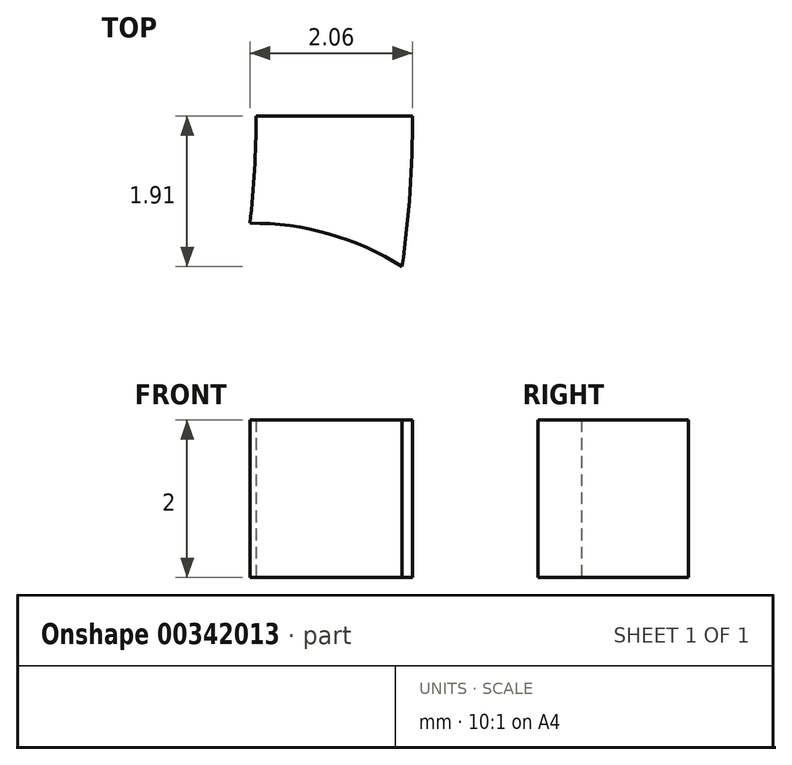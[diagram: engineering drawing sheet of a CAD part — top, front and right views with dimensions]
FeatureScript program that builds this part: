
annotation { "Feature Type Name" : "Feature", "Feature Type Description" : "" }
export const myFeature = defineFeature(function(context is Context, id is Id, definition is map)
    precondition{}
    {
        {
            var Q0;
            Q0=qCreatedBy(makeId("Top.planeOp"),FACE);
            var sketch = newSketch(context, id + "F0", { "sketchPlane" : qUnion([Q0])});
            skCircle(sketch, "E0", {"center": v(4.55, -3.95) * mm, "radius": 13.88 * mm});
            skLineSegment(sketch, "E1", {"start": v(4.55, -17.84) * mm, "end": v(4.55, 9.93) * mm});
            skLineSegment(sketch, "E2", {"start": v(-9.33, -3.95) * mm, "end": v(18.43, -3.95) * mm});
            skLineSegment(sketch, "E3", {"start": v(-9.33, -3.95) * mm, "end": v(4.55, -17.84) * mm});
            skLineSegment(sketch, "E4", {"start": v(4.55, -17.84) * mm, "end": v(18.43, -3.95) * mm});
            skLineSegment(sketch, "E5", {"start": v(18.43, -3.95) * mm, "end": v(4.55, 9.93) * mm});
            skLineSegment(sketch, "E6", {"start": v(4.55, 9.93) * mm, "end": v(-9.33, -3.95) * mm});
            skLineSegment(sketch, "E7", {"start": v(4.55, -3.95) * mm, "end": v(14.37, -13.77) * mm});
            skLineSegment(sketch, "E8", {"start": v(4.55, -3.95) * mm, "end": v(-5.27, 5.86) * mm});
            skLineSegment(sketch, "E9", {"start": v(4.55, -3.95) * mm, "end": v(-5.27, -13.77) * mm});
            skLineSegment(sketch, "E10", {"start": v(-5.27, -13.77) * mm, "end": v(4.55, -3.95) * mm});
            skLineSegment(sketch, "E11", {"start": v(4.55, -3.95) * mm, "end": v(14.37, 5.86) * mm});
            skLineSegment(sketch, "E12", {"start": v(-5.27, -13.77) * mm, "end": v(4.55, -17.84) * mm});
            skLineSegment(sketch, "E13", {"start": v(4.55, -17.84) * mm, "end": v(14.37, -13.77) * mm});
            skLineSegment(sketch, "E14", {"start": v(14.37, -13.77) * mm, "end": v(18.43, -3.95) * mm});
            skLineSegment(sketch, "E15", {"start": v(18.43, -3.95) * mm, "end": v(14.37, 5.86) * mm});
            skLineSegment(sketch, "E16", {"start": v(14.37, 5.86) * mm, "end": v(4.55, 9.93) * mm});
            skLineSegment(sketch, "E17", {"start": v(4.55, 9.93) * mm, "end": v(-5.27, 5.86) * mm});
            skLineSegment(sketch, "E18", {"start": v(-5.27, 5.86) * mm, "end": v(-9.33, -3.95) * mm});
            skLineSegment(sketch, "E19", {"start": v(-9.33, -3.95) * mm, "end": v(-5.27, -13.77) * mm});
            skCircle(sketch, "E20", {"center": v(9.46, -15.8) * mm, "radius": 3.55 * mm});
            skCircle(sketch, "E21", {"center": v(-0.36, -15.8) * mm, "radius": 3.55 * mm});
            skCircle(sketch, "E22", {"center": v(-7.3, -8.86) * mm, "radius": 3.55 * mm});
            skCircle(sketch, "E23", {"center": v(16.4, -8.86) * mm, "radius": 3.55 * mm});
            skCircle(sketch, "E24", {"center": v(16.4, 0.96) * mm, "radius": 3.55 * mm});
            skCircle(sketch, "E25", {"center": v(9.46, 7.9) * mm, "radius": 3.55 * mm});
            skCircle(sketch, "E26", {"center": v(-7.3, 0.96) * mm, "radius": 3.55 * mm});
            skLineSegment(sketch, "E27", {"start": v(26.9, 5.3) * mm, "end": v(-20.76, -14.44) * mm, "construction": true});
            skLineSegment(sketch, "E28", {"start": v(-13.05, 3.34) * mm, "end": v(23.65, -11.86) * mm, "construction": true});
            skLineSegment(sketch, "E29", {"start": v(-3.04, -22.28) * mm, "end": v(11.89, 13.76) * mm, "construction": true});
            skCircle(sketch, "E30", {"center": v(-0.36, 7.9) * mm, "radius": 3.55 * mm});
            skLineSegment(sketch, "E31", {"start": v(11.98, -21.9) * mm, "end": v(-2.96, 14.17) * mm, "construction": true});
            skSolve(sketch);
        }
        {
            var Q0;
            {var subQ3=sQuery(id+"F0.wireOp",EDGE,"E5");var subQ6=sQuery(id+"F0.wireOp",EDGE,"E24");var subQ8=makeQuery(id+"F0.imprint","INTERSECT",VERTEX,{"disambiguationData":[OD(1.0)],"derivedFrom":[subQ3,subQ6]});Q0=makeQuery(id+"F0.imprint","IMPRINT",FACE,{"disambiguationData":[TD([[makeQuery(id+"F0.imprint","IMPRINT",EDGE,{"disambiguationData":[TD([[subQ8,-1.0]])],"derivedFrom":subQ3}),1.0]])]});}
            var sketch = newSketch(context, id + "F1", { "sketchPlane" : qUnion([Q0])});
            skLineSegment(sketch, "E32.0", {"start": v(17.38, 1.36) * mm, "end": v(15.54, 0.6) * mm});
            skArc(sketch, "E32.1", {"start": v(-6.52, -12.32) * mm, "mid": v(-5.57, -11.96) * mm, "end": v(-4.77, -11.35) * mm});
            skCircle(sketch, "E32.2", {"center": v(4.55, -3.95) * mm, "radius": 13.88 * mm});
            skLineSegment(sketch, "E32.4", {"start": v(-5.27, -13.77) * mm, "end": v(-3.86, -12.36) * mm});
            skArc(sketch, "E32.6", {"start": v(2.64, -17.7) * mm, "mid": v(3.05, -16.78) * mm, "end": v(3.2, -15.77) * mm});
            skLineSegment(sketch, "E32.7", {"start": v(-0.76, -16.78) * mm, "end": v(0, -14.94) * mm});
            skLineSegment(sketch, "E32.9", {"start": v(-9.33, -3.95) * mm, "end": v(-7.34, -3.95) * mm});
            skLineSegment(sketch, "E32.11", {"start": v(-8.28, 1.36) * mm, "end": v(-6.44, 0.6) * mm});
            skLineSegment(sketch, "E32.12", {"start": v(9.86, -16.78) * mm, "end": v(9.1, -14.94) * mm});
            skLineSegment(sketch, "E32.13", {"start": v(4.55, -17.84) * mm, "end": v(4.55, -15.85) * mm});
            skArc(sketch, "E32.15", {"start": v(12.92, -15.03) * mm, "mid": v(12.56, -14.08) * mm, "end": v(11.94, -13.27) * mm});
            skArc(sketch, "E32.17", {"start": v(18.3, -5.86) * mm, "mid": v(17.37, -5.45) * mm, "end": v(16.37, -5.31) * mm});
            skLineSegment(sketch, "E32.18", {"start": v(12.96, -12.36) * mm, "end": v(14.37, -13.77) * mm});
            skArc(sketch, "E32.21", {"start": v(15.62, 4.42) * mm, "mid": v(14.67, 4.06) * mm, "end": v(13.87, 3.44) * mm});
            skLineSegment(sketch, "E32.23", {"start": v(12.96, 4.46) * mm, "end": v(14.37, 5.86) * mm});
            skArc(sketch, "E32.24", {"start": v(6.46, 9.8) * mm, "mid": v(6.04, 8.87) * mm, "end": v(5.9, 7.86) * mm});
            skArc(sketch, "E32.27", {"start": v(-9.2, -2.04) * mm, "mid": v(-8.27, -2.46) * mm, "end": v(-7.27, -2.6) * mm});
            skArc(sketch, "E32.30", {"start": v(-3.82, 7.12) * mm, "mid": v(-3.46, 6.17) * mm, "end": v(-2.85, 5.36) * mm});
            skPoint(sketch, "E33.orphan", {"position": v(-20.76, -14.44) * mm});
            skPoint(sketch, "E34.orphan", {"position": v(-3.04, -22.28) * mm});
            skPoint(sketch, "E35.orphan", {"position": v(11.98, -21.9) * mm});
            skPoint(sketch, "E36.orphan", {"position": v(23.65, -11.86) * mm});
            skPoint(sketch, "E37.orphan", {"position": v(26.9, 5.3) * mm});
            skPoint(sketch, "E38.orphan", {"position": v(11.89, 13.76) * mm});
            skPoint(sketch, "E39.orphan", {"position": v(-2.96, 14.17) * mm});
            skPoint(sketch, "E40.orphan", {"position": v(-13.05, 3.34) * mm});
            skCircle(sketch, "E41", {"center": v(4.55, -3.95) * mm, "radius": 11.9 * mm});
            skArc(sketch, "E42.trimOffspring", {"start": v(-4.77, 3.44) * mm, "mid": v(-5.57, 4.06) * mm, "end": v(-6.52, 4.42) * mm});
            skArc(sketch, "E43.trimOffspring", {"start": v(-7.27, -5.31) * mm, "mid": v(-8.27, -5.45) * mm, "end": v(-9.2, -5.86) * mm});
            skArc(sketch, "E44.trimOffspring", {"start": v(-2.85, -13.27) * mm, "mid": v(-3.46, -14.08) * mm, "end": v(-3.82, -15.03) * mm});
            skArc(sketch, "E45.trimOffspring", {"start": v(5.9, -15.77) * mm, "mid": v(6.04, -16.78) * mm, "end": v(6.46, -17.7) * mm});
            skArc(sketch, "E46.trimOffspring", {"start": v(13.87, -11.35) * mm, "mid": v(14.67, -11.96) * mm, "end": v(15.62, -12.32) * mm});
            skArc(sketch, "E47.trimOffspring", {"start": v(16.37, -2.6) * mm, "mid": v(17.37, -2.46) * mm, "end": v(18.3, -2.04) * mm});
            skArc(sketch, "E48.trimOffspring", {"start": v(11.94, 5.36) * mm, "mid": v(12.56, 6.17) * mm, "end": v(12.92, 7.12) * mm});
            skArc(sketch, "E49.trimOffspring", {"start": v(3.2, 7.86) * mm, "mid": v(3.05, 8.87) * mm, "end": v(2.64, 9.8) * mm});
            skPoint(sketch, "E50", {"position": v(0, 7.04) * mm});
            skPoint(sketch, "E51", {"position": v(9.1, 7.04) * mm});
            skPoint(sketch, "E52", {"position": v(12.96, 4.46) * mm});
            skPoint(sketch, "E53", {"position": v(15.54, 0.6) * mm});
            skPoint(sketch, "E54", {"position": v(16.44, -3.95) * mm});
            skPoint(sketch, "E55", {"position": v(15.54, -8.5) * mm});
            skPoint(sketch, "E56", {"position": v(12.96, -12.36) * mm});
            skPoint(sketch, "E57", {"position": v(9.1, -14.94) * mm});
            skPoint(sketch, "E58", {"position": v(4.55, -15.85) * mm});
            skPoint(sketch, "E59", {"position": v(0, -14.94) * mm});
            skPoint(sketch, "E60", {"position": v(-3.86, -12.36) * mm});
            skPoint(sketch, "E61", {"position": v(-6.44, -8.5) * mm});
            skPoint(sketch, "E62", {"position": v(-7.34, -3.95) * mm});
            skPoint(sketch, "E63", {"position": v(-6.44, 0.6) * mm});
            skPoint(sketch, "E64", {"position": v(-3.86, 4.46) * mm});
            skLineSegment(sketch, "E65.trimOffspring", {"start": v(0, 7.04) * mm, "end": v(-0.76, 8.87) * mm});
            skLineSegment(sketch, "E66.trimOffspring", {"start": v(4.55, 7.94) * mm, "end": v(4.55, 9.93) * mm});
            skLineSegment(sketch, "E67.trimOffspring", {"start": v(9.1, 7.04) * mm, "end": v(9.86, 8.87) * mm});
            skLineSegment(sketch, "E68.trimOffspring", {"start": v(-6.44, -8.5) * mm, "end": v(-8.28, -9.27) * mm});
            skLineSegment(sketch, "E69.trimOffspring", {"start": v(16.44, -3.95) * mm, "end": v(18.43, -3.95) * mm});
            skLineSegment(sketch, "E70.trimOffspring", {"start": v(15.54, -8.5) * mm, "end": v(17.38, -9.27) * mm});
            skLineSegment(sketch, "E71.trimOffspring", {"start": v(-3.86, 4.46) * mm, "end": v(-5.27, 5.86) * mm});
            skSolve(sketch);
        }
        {
            var Q0;
            {var subQ33=sQuery(id+"F1.wireOp",EDGE,"E69.trimOffspring");Q0=makeQuery(id+"F1.imprint","IMPRINT",FACE,{"disambiguationData":[TD([[makeQuery(id+"F1.imprint","IMPRINT",EDGE,{"derivedFrom":subQ33}),-1.0]])]});}
            extrude(context, id + "F2", {"entities" : qUnion([Q0]), "depth" : 2 * mm});
        }
    });
